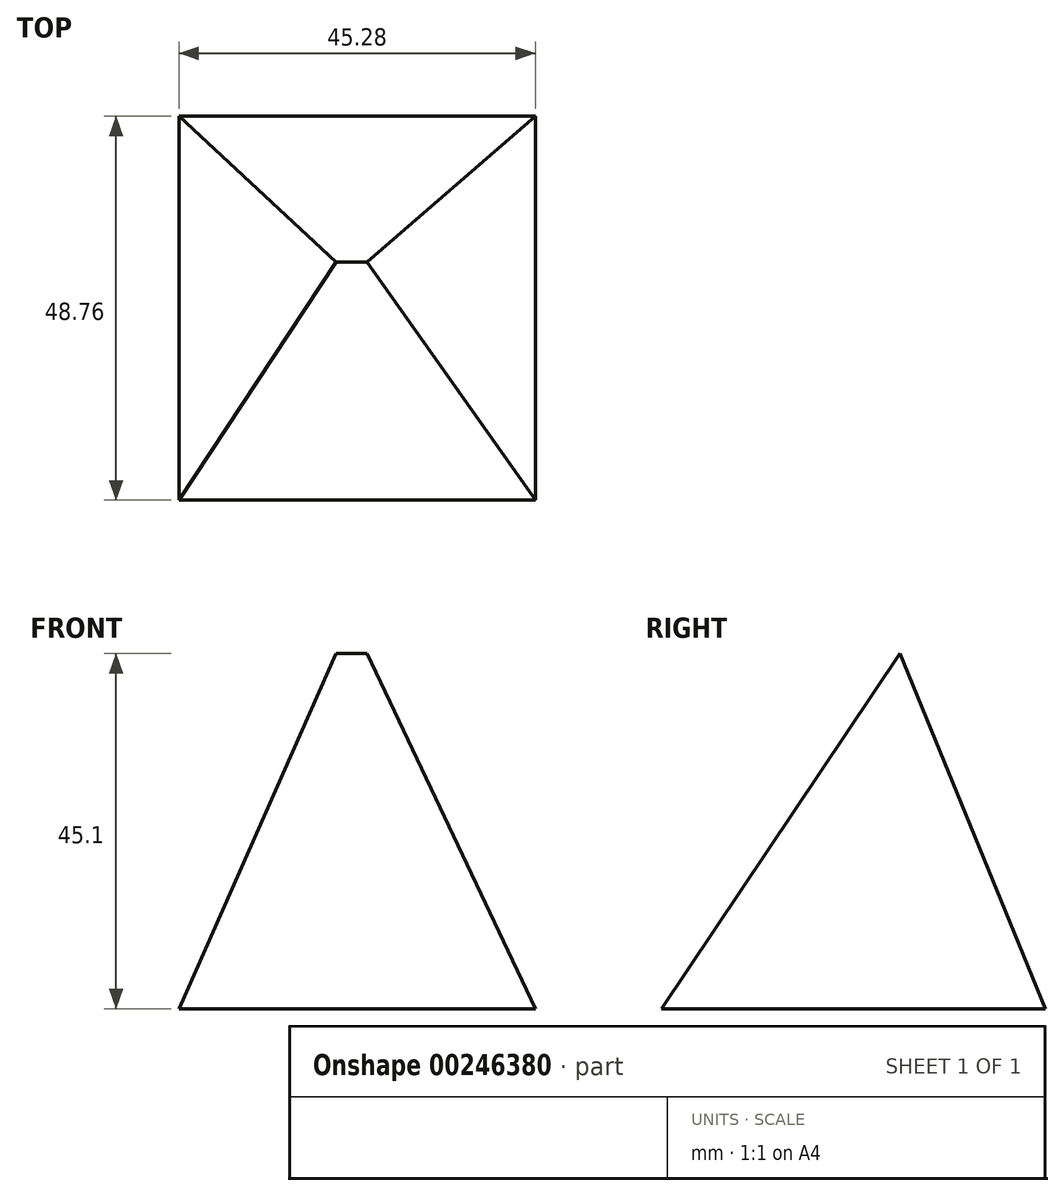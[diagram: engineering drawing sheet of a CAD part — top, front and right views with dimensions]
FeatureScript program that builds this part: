
annotation { "Feature Type Name" : "Feature", "Feature Type Description" : "" }
export const myFeature = defineFeature(function(context is Context, id is Id, definition is map)
    precondition{}
    {
        {
            var Q0;
            Q0=qCreatedBy(makeId("Front.planeOp"),FACE);
            var sketch = newSketch(context, id + "F0", { "sketchPlane" : qUnion([Q0])});
            skLineSegment(sketch, "E0.bottom", {"start": v(-29.49, 0) * mm, "end": v(26.07, 0) * mm});
            skLineSegment(sketch, "E0.top", {"start": v(-29.49, 56.53) * mm, "end": v(26.07, 56.53) * mm});
            skLineSegment(sketch, "E0.left", {"start": v(-29.49, 0) * mm, "end": v(-29.49, 56.53) * mm});
            skLineSegment(sketch, "E0.right", {"start": v(26.07, 0) * mm, "end": v(26.07, 56.53) * mm});
            skSolve(sketch);
        }
        {
            var Q0;
            Q0=makeQuery(id+"F0.imprint","IMPRINT",FACE,{"disambiguationData":[TD([[makeQuery(id+"F0.imprint","IMPRINT",EDGE,{"derivedFrom":sQuery(id+"F0.wireOp",EDGE,"E0.bottom")}),1.0]])]});
            extrude(context, id + "F1", {"entities" : qUnion([Q0]), "depth" : 55.88 * mm});
        }
        {
            var Q0;
            Q0=qCreatedBy(makeId("Front.planeOp"),FACE);
            var sketch = newSketch(context, id + "F2", { "sketchPlane" : qUnion([Q0])});
            skLineSegment(sketch, "E1", {"start": v(27.56, 0) * mm, "end": v(27.56, 58.05) * mm});
            skLineSegment(sketch, "E2", {"start": v(27.56, 58.05) * mm, "end": v(0, 58.05) * mm});
            skLineSegment(sketch, "E3", {"start": v(0, 58.05) * mm, "end": v(27.56, 0) * mm});
            skSolve(sketch);
        }
        {
            var Q0;
            Q0=makeQuery(id+"F2.imprint","IMPRINT",FACE,{"disambiguationData":[TD([[makeQuery(id+"F2.imprint","IMPRINT",EDGE,{"derivedFrom":sQuery(id+"F2.wireOp",EDGE,"E1")}),1.0]])]});
            extrude(context, id + "F3", {"entities" : qUnion([Q0]), "operationType" : NewBodyOperationType.REMOVE, "depth" : 143.76 * mm});
        }
        {
            var Q0;
            Q0=qCreatedBy(makeId("Right.planeOp"),FACE);
            var sketch = newSketch(context, id + "F4", { "sketchPlane" : qUnion([Q0])});
            skLineSegment(sketch, "E4", {"start": v(-61.12, 0) * mm, "end": v(-15.73, 67.62) * mm});
            skLineSegment(sketch, "E5", {"start": v(-15.73, 67.62) * mm, "end": v(-62.02, 67.62) * mm});
            skLineSegment(sketch, "E6", {"start": v(-62.02, 67.62) * mm, "end": v(-61.12, 0) * mm});
            skSolve(sketch);
        }
        {
            var Q0;
            Q0=makeQuery(id+"F4.imprint","IMPRINT",FACE,{"disambiguationData":[TD([[makeQuery(id+"F4.imprint","IMPRINT",EDGE,{"derivedFrom":sQuery(id+"F4.wireOp",EDGE,"E4")}),1.0]])]});
            extrude(context, id + "F5", {"entities" : qUnion([Q0]), "operationType" : NewBodyOperationType.REMOVE, "endBound" : BoundingType.SYMMETRIC, "depth" : 90.93 * mm});
        }
        {
            var Q0;
            Q0=makeQuery(id+"F1.opExtrude","SWEPT_FACE",FACE,{"disambiguationData":[OSD([sQuery(id+"F0.wireOp",EDGE,"E0.left")])]});
            var sketch = newSketch(context, id + "F6", { "sketchPlane" : qUnion([Q0])});
            skLineSegment(sketch, "E7", {"start": v(23.18, 56.53) * mm, "end": v(0, 0) * mm});
            skLineSegment(sketch, "E8", {"start": v(0, 0) * mm, "end": v(0, 56.53) * mm});
            skLineSegment(sketch, "E9", {"start": v(0, 56.53) * mm, "end": v(23.18, 56.53) * mm});
            skSolve(sketch);
        }
        {
            var Q0;
            Q0=makeQuery(id+"F6.imprint","IMPRINT",FACE,{"disambiguationData":[TD([[makeQuery(id+"F6.imprint","IMPRINT",EDGE,{"derivedFrom":sQuery(id+"F6.wireOp",EDGE,"E7")}),-1.0]])]});
            extrude(context, id + "F7", {"entities" : qUnion([Q0]), "operationType" : NewBodyOperationType.REMOVE, "oppositeDirection" : true, "depth" : 94.74 * mm});
        }
        {
            var Q0;
            Q0=qCreatedBy(makeId("Front.planeOp"),FACE);
            var sketch = newSketch(context, id + "F8", { "sketchPlane" : qUnion([Q0])});
            skLineSegment(sketch, "E10", {"start": v(-28.2, 0) * mm, "end": v(0, 63.73) * mm});
            skLineSegment(sketch, "E11", {"start": v(0, 63.73) * mm, "end": v(-39.34, 63.73) * mm});
            skLineSegment(sketch, "E12", {"start": v(-39.34, 63.73) * mm, "end": v(-28.2, 0) * mm});
            skSolve(sketch);
        }
        {
            var Q0;
            Q0=makeQuery(id+"F8.imprint","IMPRINT",FACE,{"disambiguationData":[TD([[makeQuery(id+"F8.imprint","IMPRINT",EDGE,{"derivedFrom":sQuery(id+"F8.wireOp",EDGE,"E10")}),1.0]])]});
            extrude(context, id + "F9", {"entities" : qUnion([Q0]), "operationType" : NewBodyOperationType.REMOVE, "depth" : 254 * mm});
        }
        {
            var Q0;
            Q0=qCreatedBy(makeId("Front.planeOp"),FACE);
            var sketch = newSketch(context, id + "F10", { "sketchPlane" : qUnion([Q0])});
            skLineSegment(sketch, "E13.bottom", {"start": v(44.72, -25.3) * mm, "end": v(-58.13, -25.3) * mm});
            skLineSegment(sketch, "E13.top", {"start": v(44.72, 8.33) * mm, "end": v(-58.13, 8.33) * mm});
            skLineSegment(sketch, "E13.left", {"start": v(44.72, -25.3) * mm, "end": v(44.72, 8.33) * mm});
            skLineSegment(sketch, "E13.right", {"start": v(-58.13, -25.3) * mm, "end": v(-58.13, 8.33) * mm});
            skSolve(sketch);
        }
        {
            var Q0;
            Q0 = qSketchRegion(id + "F10", true);
            extrude(context, id + "F11", {"entities" : qUnion([Q0]), "operationType" : NewBodyOperationType.REMOVE, "depth" : 128.52 * mm});
        }
        {
            var Q0;
            Q0=qCreatedBy(makeId("Top.planeOp"),FACE);
            var sketch = newSketch(context, id + "F12", { "sketchPlane" : qUnion([Q0])});
            skLineSegment(sketch, "E14.bottom", {"start": v(76.5, -60.55) * mm, "end": v(-51.5, -60.55) * mm});
            skLineSegment(sketch, "E14.top", {"start": v(76.5, 27.88) * mm, "end": v(-51.5, 27.88) * mm});
            skLineSegment(sketch, "E14.left", {"start": v(76.5, -60.55) * mm, "end": v(76.5, 27.88) * mm});
            skLineSegment(sketch, "E14.right", {"start": v(-51.5, -60.55) * mm, "end": v(-51.5, 27.88) * mm});
            skSolve(sketch);
        }
        {
            var Q0;
            Q0 = qSketchRegion(id + "F12", true);
            extrude(context, id + "F13", {"entities" : qUnion([Q0]), "operationType" : NewBodyOperationType.REMOVE, "depth" : 11.43 * mm});
        }
    });
